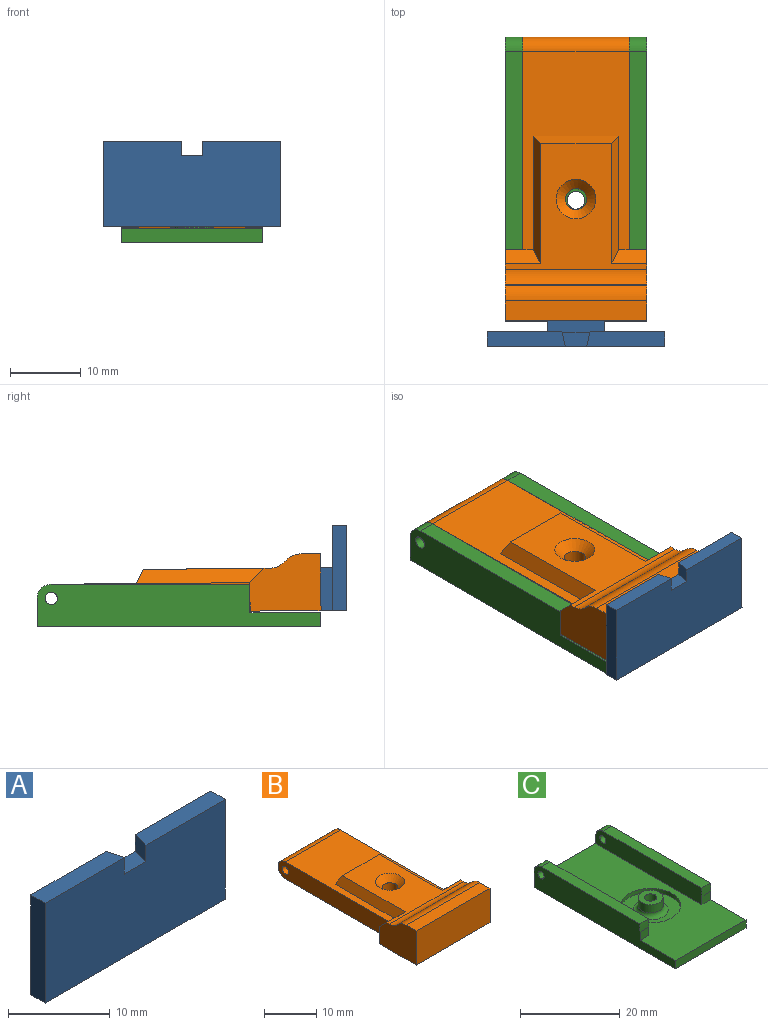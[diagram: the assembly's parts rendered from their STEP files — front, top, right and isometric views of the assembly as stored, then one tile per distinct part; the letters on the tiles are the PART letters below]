
ASSEMBLY  parts=3 mates=3
PART A: 15 faces, bbox 25x7x12 mm
  f0: plane 12x2mm, normal (-1,0,0), area 24mm2, adj f1,f5,f6,f7
  f1: plane 25x7mm, normal (0,0,-1), area 90mm2, adj f0,f2,f6,f7,f8,f11,f12
  f2: plane 12x2mm, normal (1,0,0), area 24mm2, adj f1,f3,f6,f7
  f3: plane 11x2mm, normal (0,0,1), area 21.5mm2, adj f2,f6,f7,f13
  f4: plane 4x2mm, normal (0,0,1), area 7mm2, adj f6,f7,f13,f14
  f5: plane 11x2mm, normal (0,0,1), area 21.5mm2, adj f0,f6,f7,f14
  f6: plane 25x12mm, normal (0,1,0), area 244mm2, adj f0,f1,f2,f3,f4,f5,f10,f11
  f7: plane 25x12mm, normal (0,-1,0), area 294mm2, adj f0,f1,f2,f3,f4,f5,f13,f14
  f8: plane 8x3mm, normal (0,1,0), area 24mm2, adj f1,f9,f11,f12
  f9: plane 8x3mm, normal (0,0.71,0.71), area 33.9mm2, adj f8,f10,f11,f12
  f10: plane 8x2mm, normal (0,0,1), area 16mm2, adj f6,f9,f11,f12
  f11: plane 6x5mm, normal (1,0,0), area 25.5mm2, adj f1,f6,f8,f9,f10
  f12: plane 6x5mm, normal (-1,0,0), area 25.5mm2, adj f1,f6,f8,f9,f10
  f13: plane 2x2mm, normal (-0.97,0.24,0), area 4.1mm2, adj f3,f4,f6,f7
  f14: plane 2x2mm, normal (0.97,0.24,0), area 4.1mm2, adj f4,f5,f6,f7
PART B: 25 faces, bbox 20x40x8 mm
  f0: plane 20x17.76mm, normal (0,0,1), area 160.5mm2, adj f9,f11,f12,f13,f14,f15,f16,f19
  f1: plane 30x4mm, normal (1,0,0), area 115.9mm2, adj f3,f4,f5,f6,f8
  f2: plane 30x4mm, normal (-1,0,0), area 115.9mm2, adj f3,f4,f5,f6,f7
  f3: plane 28x15mm, normal (0,0,1), area 228mm2, adj f1,f2,f6,f12,f13,f14,f15,f16
  f4: plane 38x20mm, normal (0,0,-1), area 591.7mm2, adj f1,f2,f6,f7,f8,f9,f10,f11
  f5: cylinder r=0.88mm len=15mm, axis (1,0,0), area 82.5mm2, adj f1,f2
  f6: cylinder r=2mm len=15mm, axis (1,0,0), area 94.2mm2, adj f1,f2,f3,f4
  f7: plane 4x2.5mm, normal (0,1,0), area 10mm2, adj f2,f4,f9,f12
  f8: plane 4x2.5mm, normal (0,1,0), area 10mm2, adj f1,f4,f11,f13
  f9: plane 10x8mm, normal (-1,0,0), area 68mm2, adj f0,f4,f7,f10,f12,f21,f22,f23
  f10: plane 20x8mm, normal (0,-1,0), area 160mm2, adj f4,f9,f11,f21
  f11: plane 10x8mm, normal (1,0,0), area 68mm2, adj f0,f4,f8,f10,f13,f21,f22,f23
  f12: plane 5x2mm, normal (0,0.71,0.71), area 12.7mm2, adj f0,f3,f7,f9,f15
  f13: plane 5x2mm, normal (0,0.71,0.71), area 12.7mm2, adj f0,f3,f8,f11,f14
  f14: plane 18x2mm, normal (0.89,0,0.45), area 36.9mm2, adj f0,f3,f13,f16
  f15: plane 18x2mm, normal (-0.89,0,0.45), area 36.9mm2, adj f0,f3,f12,f16
  f16: plane 12x2mm, normal (0,0.89,0.45), area 24.6mm2, adj f0,f3,f14,f15
  f17: plane 6x6mm, normal (0,0,-1), area 21.2mm2, adj f18,f20
  f18: cylinder r=1.5mm len=3mm, axis (0,0,-1), area 25.4mm2, adj f17,f19
  f19: cone r=2.8mm half-angle=45deg, axis (0,0,1), area 24.8mm2, adj f0,f18
  f20: cylinder r=3mm len=6mm, axis (0,0,-1), area 37.7mm2, adj f4,f17
  f21: plane 20x2.76mm, normal (0,0,1), area 55.1mm2, adj f9,f10,f11,f23
  f22: plane 20x0.24mm, normal (0,0.71,0.71), area 6.9mm2, adj f9,f11,f23,f24
  f23: cylinder r=3mm len=20mm, axis (1,0,0), area 47.1mm2, adj f9,f11,f21,f22
  f24: cylinder r=3mm len=20mm, axis (1,0,0), area 47.1mm2, adj f0,f9,f11,f22
PART C: 24 faces, bbox 20x40x6 mm
  f0: plane 30x4mm, normal (-1,0,0), area 116.7mm2, adj f4,f7,f9,f10,f11,f12,f23
  f1: plane 30x4mm, normal (1,0,0), area 116.7mm2, adj f4,f5,f9,f13,f14,f15,f22
  f2: plane 40x6mm, normal (-1,0,0), area 196.7mm2, adj f4,f5,f6,f8,f9,f13,f14,f15
  f3: plane 40x6mm, normal (1,0,0), area 196.7mm2, adj f4,f6,f7,f8,f9,f10,f11,f12
  f4: plane 40x20mm, normal (0,0,1), area 536.9mm2, adj f0,f1,f2,f3,f8,f9,f10,f14
  f5: plane 27.93x2.5mm, normal (0,0,1), area 69.8mm2, adj f1,f2,f13,f22
  f6: plane 40x20mm, normal (0,0,-1), area 795.1mm2, adj f2,f3,f8,f9,f21
  f7: plane 27.93x2.5mm, normal (0,0,1), area 69.8mm2, adj f0,f3,f11,f23
  f8: plane 20x2mm, normal (0,-1,0), area 40mm2, adj f2,f3,f4,f6
  f9: plane 20x4mm, normal (0,1,0), area 50mm2, adj f0,f1,f2,f3,f4,f6,f22,f23
  f10: plane 2.5x2mm, normal (0,-1,0), area 5mm2, adj f0,f3,f4,f11
  f11: cylinder r=28mm len=2.5mm, axis (1,0,0), area 5mm2, adj f0,f3,f7,f10
  f12: cylinder r=0.88mm len=2.5mm, axis (1,0,0), area 13.7mm2, adj f0,f3
  f13: cylinder r=28mm len=2.5mm, axis (1,0,0), area 5mm2, adj f1,f2,f5,f14
  f14: plane 2.5x2mm, normal (0,-1,0), area 5mm2, adj f1,f2,f4,f13
  f15: cylinder r=0.88mm len=2.5mm, axis (1,0,0), area 13.7mm2, adj f1,f2
  f16: cylinder r=6mm len=12mm, axis (0,0,1), area 37.7mm2, adj f4,f17
  f17: plane 12x12mm, normal (0,0,1), area 74.6mm2, adj f16,f20
  f18: cylinder r=2.5mm len=5mm, axis (0,0,-1), area 31.4mm2, adj f19,f20
  f19: plane 5x5mm, normal (0,0,1), area 14.7mm2, adj f18,f21
  f20: torus R=3.5mm, axis (0,0,1), area 28.3mm2, adj f17,f18
  f21: cylinder r=1.25mm len=4mm, axis (0,0,1), area 31.4mm2, adj f6,f19
  f22: cylinder r=2mm len=2.5mm, axis (-1,0,0), area 7.9mm2, adj f1,f2,f5,f9
  f23: cylinder r=2mm len=2.5mm, axis (-1,0,0), area 7.9mm2, adj f0,f3,f7,f9
PLACE A rot(axis=(-1,0,0),0.5deg) t=(0.1,-23.67,-0.77)mm
PLACE B rot(axis=(-1,0,0),0.5deg) t=(0.1,4.98,-0.99)mm
PLACE C t=(0.1,0,-0.09)mm fixed
MATE cylindrical C.f23 <-> B.f5  axis (1,0,0) through (10.1,18,0.91)mm
MATE planar B.f1 <-> C.f0  axis (1,0,0) through (7.6,4.01,3.02)mm
MATE fastened A.f1 <-> B.f4  axis (0,-0.01,-1) through (0.1,-21.11,-0.79)mm
